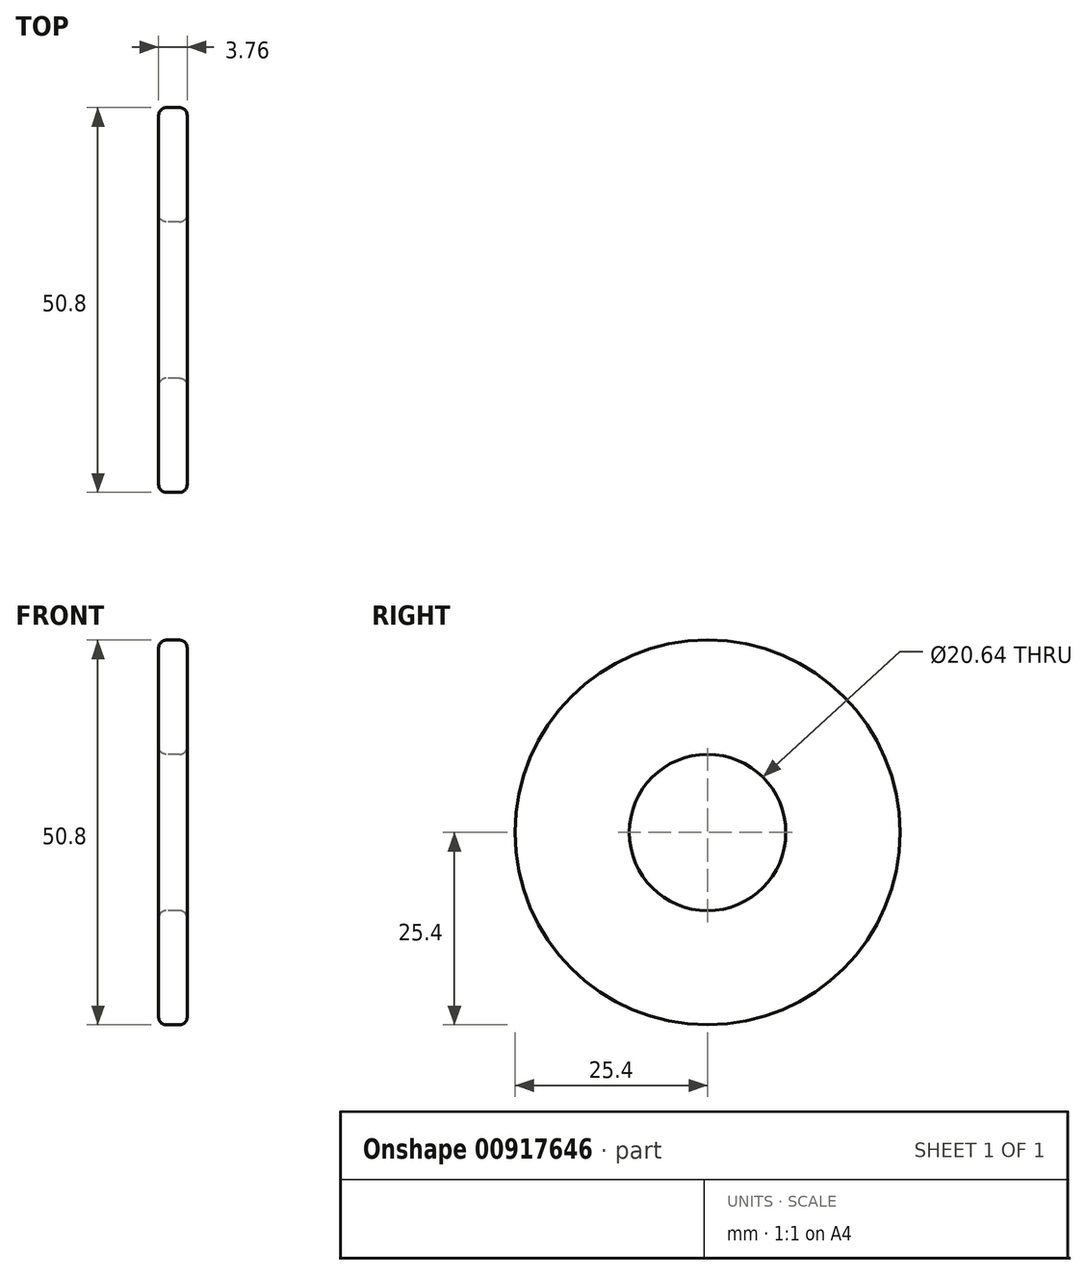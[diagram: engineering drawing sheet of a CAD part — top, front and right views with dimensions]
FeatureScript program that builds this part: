
annotation { "Feature Type Name" : "Feature", "Feature Type Description" : "" }
export const myFeature = defineFeature(function(context is Context, id is Id, definition is map)
    precondition{}
    {
        {
            var Q0;
            Q0=qCreatedBy(makeId("Right.planeOp"),FACE);
            var sketch = newSketch(context, id + "F0", { "sketchPlane" : qUnion([Q0])});
            skCircle(sketch, "E0", {"center": v(0, 0) * mm, "radius": 25.4 * mm});
            skCircle(sketch, "E1", {"center": v(0, 0) * mm, "radius": 10.32 * mm});
            skSolve(sketch);
        }
        {
            var Q0;
            Q0 = qSketchRegion(id + "F0", true);
            extrude(context, id + "F1", {"entities" : qUnion([Q0]), "depth" : 3.76 * mm, "offsetDistance" : 25.4 * mm});
        }
        {
            var Q0;
            Q0=makeQuery(id+"F1.opExtrude","CAP_EDGE",EDGE,{"disambiguationData":[OSD([sQuery(id+"F0.wireOp",EDGE,"E0")])],"isStart":false});
            var Q1;
            Q1=makeQuery(id+"F1.opExtrude","CAP_EDGE",EDGE,{"disambiguationData":[OSD([sQuery(id+"F0.wireOp",EDGE,"E0")])],"isStart":true});
            var Q2;
            Q2=makeQuery(id+"F1.opExtrude","CAP_EDGE",EDGE,{"disambiguationData":[OSD([sQuery(id+"F0.wireOp",EDGE,"E1")])],"isStart":false});
            var Q3;
            Q3=makeQuery(id+"F1.opExtrude","CAP_EDGE",EDGE,{"disambiguationData":[OSD([sQuery(id+"F0.wireOp",EDGE,"E1")])],"isStart":true});
            fillet(context, id + "F2", {"entities" : qUnion([Q0, Q1, Q2, Q3]), "tangentPropagation" : true, "radius" : 1.02 * mm, "defaultsChanged" : false, "vertexSettings" : [], "allowEdgeOverflow" : false});
        }
    });
